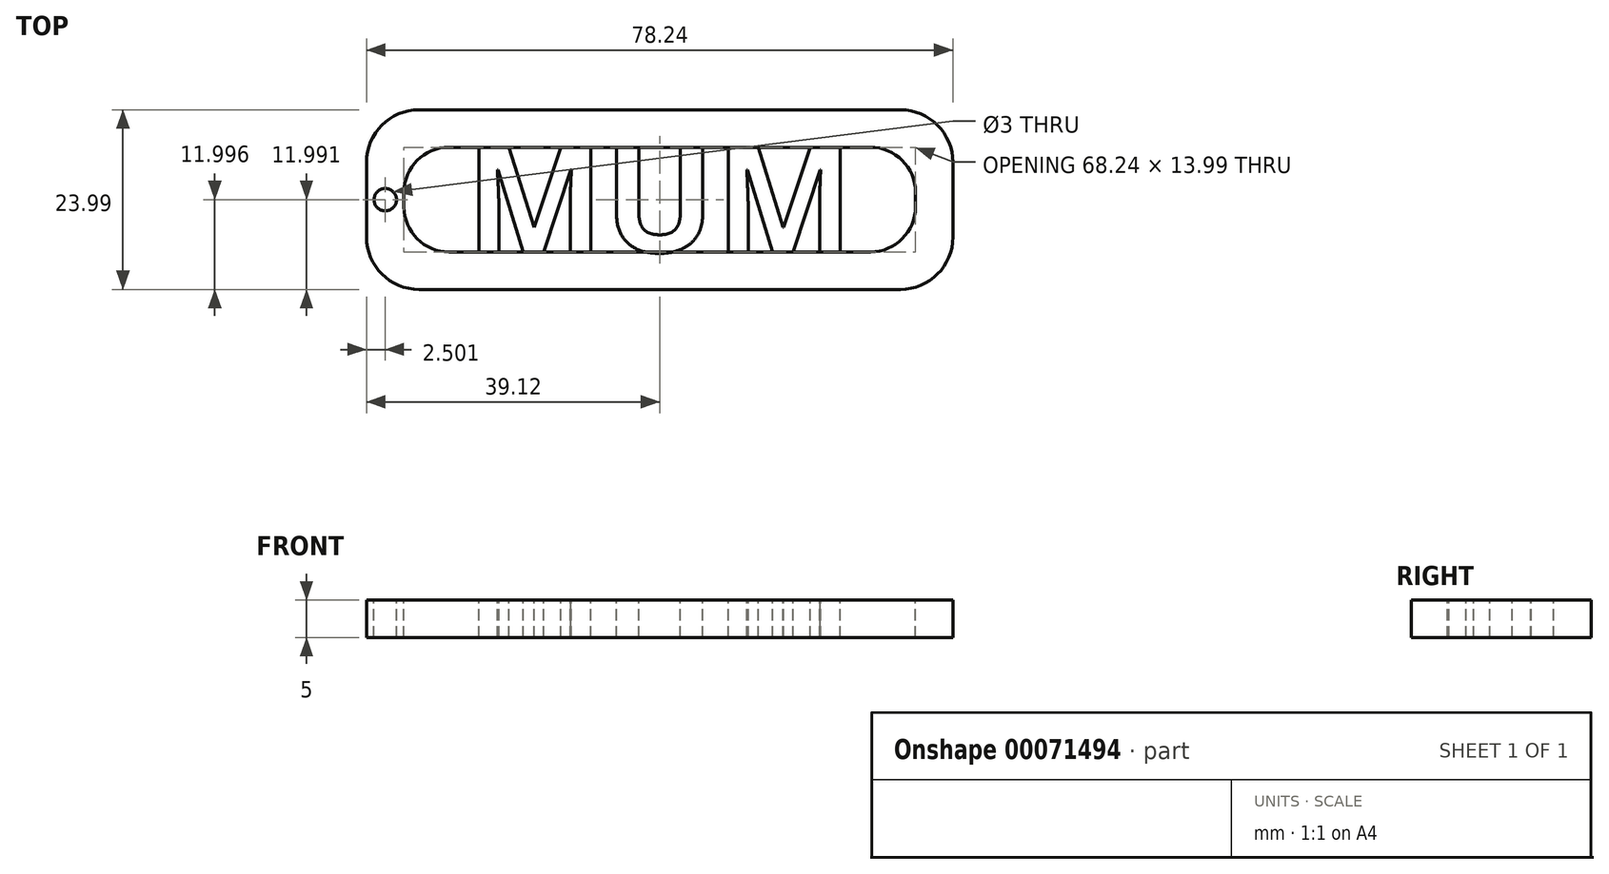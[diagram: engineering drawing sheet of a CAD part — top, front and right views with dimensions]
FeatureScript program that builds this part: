
annotation { "Feature Type Name" : "Feature", "Feature Type Description" : "" }
export const myFeature = defineFeature(function(context is Context, id is Id, definition is map)
    precondition{}
    {
        {
            var Q0;
            Q0=qCreatedBy(makeId("Top.planeOp"),FACE);
            var sketch = newSketch(context, id + "F0", { "sketchPlane" : qUnion([Q0])});
            skText(sketch, "E0", { "text": "MUM", "fontName": "OpenSans-Bold.ttf"});
            const initialGuessF0  = {"E0": [0, -0.0141, 1, 0, 0.0141]};
            skSetInitialGuess(sketch, initialGuessF0);
            skSolve(sketch);
        }
        {
            var Q0;
            Q0=qSketchRegion(id+"F0",true);
            extrude(context, id + "F1", {"entities" : qUnion([Q0]), "oppositeDirection" : true, "depth" : 5 * mm});
        }
        {
            var Q0;
            Q0=makeQuery(id+"F1.opExtrude","CAP_FACE",FACE,{"disambiguationData":[OSD([sQuery(id+"F0.wireOp",EDGE,"E0.sketch_text.stroke-34"),sQuery(id+"F0.wireOp",EDGE,"E0.sketch_text.stroke-35"),sQuery(id+"F0.wireOp",EDGE,"E0.sketch_text.stroke-36"),sQuery(id+"F0.wireOp",EDGE,"E0.sketch_text.stroke-37"),sQuery(id+"F0.wireOp",EDGE,"E0.sketch_text.stroke-38"),sQuery(id+"F0.wireOp",EDGE,"E0.sketch_text.stroke-39"),sQuery(id+"F0.wireOp",EDGE,"E0.sketch_text.stroke-40"),sQuery(id+"F0.wireOp",EDGE,"E0.sketch_text.stroke-41"),sQuery(id+"F0.wireOp",EDGE,"E0.sketch_text.stroke-42"),sQuery(id+"F0.wireOp",EDGE,"E0.sketch_text.stroke-43"),sQuery(id+"F0.wireOp",EDGE,"E0.sketch_text.stroke-44"),sQuery(id+"F0.wireOp",EDGE,"E0.sketch_text.stroke-45"),sQuery(id+"F0.wireOp",EDGE,"E0.sketch_text.stroke-46"),sQuery(id+"F0.wireOp",EDGE,"E0.sketch_text.stroke-47"),sQuery(id+"F0.wireOp",EDGE,"E0.sketch_text.stroke-48"),sQuery(id+"F0.wireOp",EDGE,"E0.sketch_text.stroke-49"),sQuery(id+"F0.wireOp",EDGE,"E0.sketch_text.stroke-50"),sQuery(id+"F0.wireOp",EDGE,"E0.sketch_text.stroke-51"),sQuery(id+"F0.wireOp",EDGE,"E0.sketch_text.stroke-52")])],"isStart":true});
            var sketch = newSketch(context, id + "F2", { "sketchPlane" : qUnion([Q0])});
            skLineSegment(sketch, "E1.bottom", {"start": v(-8.24, -0.12) * mm, "end": v(60, -0.12) * mm});
            skLineSegment(sketch, "E1.top", {"start": v(-8.24, -14.1) * mm, "end": v(60, -14.1) * mm});
            skLineSegment(sketch, "E1.left", {"start": v(-8.24, -0.12) * mm, "end": v(-8.24, -14.1) * mm});
            skLineSegment(sketch, "E1.right", {"start": v(60, -0.12) * mm, "end": v(60, -14.1) * mm});
            skLineSegment(sketch, "E2.bottom", {"start": v(-13.24, 4.88) * mm, "end": v(65, 4.88) * mm});
            skLineSegment(sketch, "E2.top", {"start": v(-13.24, -19.1) * mm, "end": v(65, -19.1) * mm});
            skLineSegment(sketch, "E2.left", {"start": v(-13.24, 4.88) * mm, "end": v(-13.24, -19.1) * mm});
            skLineSegment(sketch, "E2.right", {"start": v(65, 4.88) * mm, "end": v(65, -19.1) * mm});
            skSolve(sketch);
        }
        {
            var Q0;
            Q0 = qSketchRegion(id + "F2", true);
            extrude(context, id + "F3", {"entities" : qUnion([Q0]), "oppositeDirection" : true, "depth" : 5 * mm});
        }
        {
            var Q0;
            Q0=makeQuery(id+"F3.opExtrude","SWEPT_EDGE",EDGE,{"disambiguationData":[OSD([sQuery(id+"F2.wireOp",EDGE,"E1.bottom"),sQuery(id+"F2.wireOp",EDGE,"E1.left")])]});
            var Q1;
            Q1=makeQuery(id+"F3.opExtrude","SWEPT_EDGE",EDGE,{"disambiguationData":[OSD([sQuery(id+"F2.wireOp",EDGE,"E1.top"),sQuery(id+"F2.wireOp",EDGE,"E1.left")])]});
            var Q2;
            Q2=makeQuery(id+"F3.opExtrude","SWEPT_EDGE",EDGE,{"disambiguationData":[OSD([sQuery(id+"F2.wireOp",EDGE,"E1.bottom"),sQuery(id+"F2.wireOp",EDGE,"E1.right")])]});
            var Q3;
            Q3=makeQuery(id+"F3.opExtrude","SWEPT_EDGE",EDGE,{"disambiguationData":[OSD([sQuery(id+"F2.wireOp",EDGE,"E1.top"),sQuery(id+"F2.wireOp",EDGE,"E1.right")])]});
            fillet(context, id + "F4", {"entities" : qUnion([Q0, Q1, Q2, Q3]), "radius" : 6 * mm, "tangentPropagation" : true, "allowEdgeOverflow" : false});
        }
        {
            var Q0;
            Q0=makeQuery(id+"F3.opExtrude","SWEPT_EDGE",EDGE,{"disambiguationData":[OSD([sQuery(id+"F2.wireOp",EDGE,"E2.top"),sQuery(id+"F2.wireOp",EDGE,"E2.left")])]});
            var Q1;
            Q1=makeQuery(id+"F3.opExtrude","SWEPT_EDGE",EDGE,{"disambiguationData":[OSD([sQuery(id+"F2.wireOp",EDGE,"E2.bottom"),sQuery(id+"F2.wireOp",EDGE,"E2.right")])]});
            var Q2;
            Q2=makeQuery(id+"F3.opExtrude","SWEPT_EDGE",EDGE,{"disambiguationData":[OSD([sQuery(id+"F2.wireOp",EDGE,"E2.top"),sQuery(id+"F2.wireOp",EDGE,"E2.right")])]});
            var Q3;
            Q3=makeQuery(id+"F3.opExtrude","SWEPT_EDGE",EDGE,{"disambiguationData":[OSD([sQuery(id+"F2.wireOp",EDGE,"E2.bottom"),sQuery(id+"F2.wireOp",EDGE,"E2.left")])]});
            fillet(context, id + "F5", {"entities" : qUnion([Q0, Q1, Q2, Q3]), "radius" : 7 * mm, "tangentPropagation" : true, "allowEdgeOverflow" : false});
        }
        {
            var Q0;
            Q0=makeQuery(id+"F3.opExtrude","CAP_FACE",FACE,{"disambiguationData":[OSD([sQuery(id+"F2.wireOp",EDGE,"E1.bottom"),sQuery(id+"F2.wireOp",EDGE,"E1.top"),sQuery(id+"F2.wireOp",EDGE,"E1.left"),sQuery(id+"F2.wireOp",EDGE,"E1.right"),sQuery(id+"F2.wireOp",EDGE,"E2.bottom"),sQuery(id+"F2.wireOp",EDGE,"E2.top"),sQuery(id+"F2.wireOp",EDGE,"E2.left"),sQuery(id+"F2.wireOp",EDGE,"E2.right")])],"isStart":true});
            var sketch = newSketch(context, id + "F6", { "sketchPlane" : qUnion([Q0])});
            skCircle(sketch, "E3", {"center": v(-10.74, -7.12) * mm, "radius": 1.5 * mm});
            skSolve(sketch);
        }
        {
            var Q0;
            Q0 = qSketchRegion(id + "F6", true);
            extrude(context, id + "F7", {"entities" : qUnion([Q0]), "operationType" : NewBodyOperationType.REMOVE, "endBound" : BoundingType.THROUGH_ALL, "oppositeDirection" : true, "depth" : 25 * mm});
        }
    });
